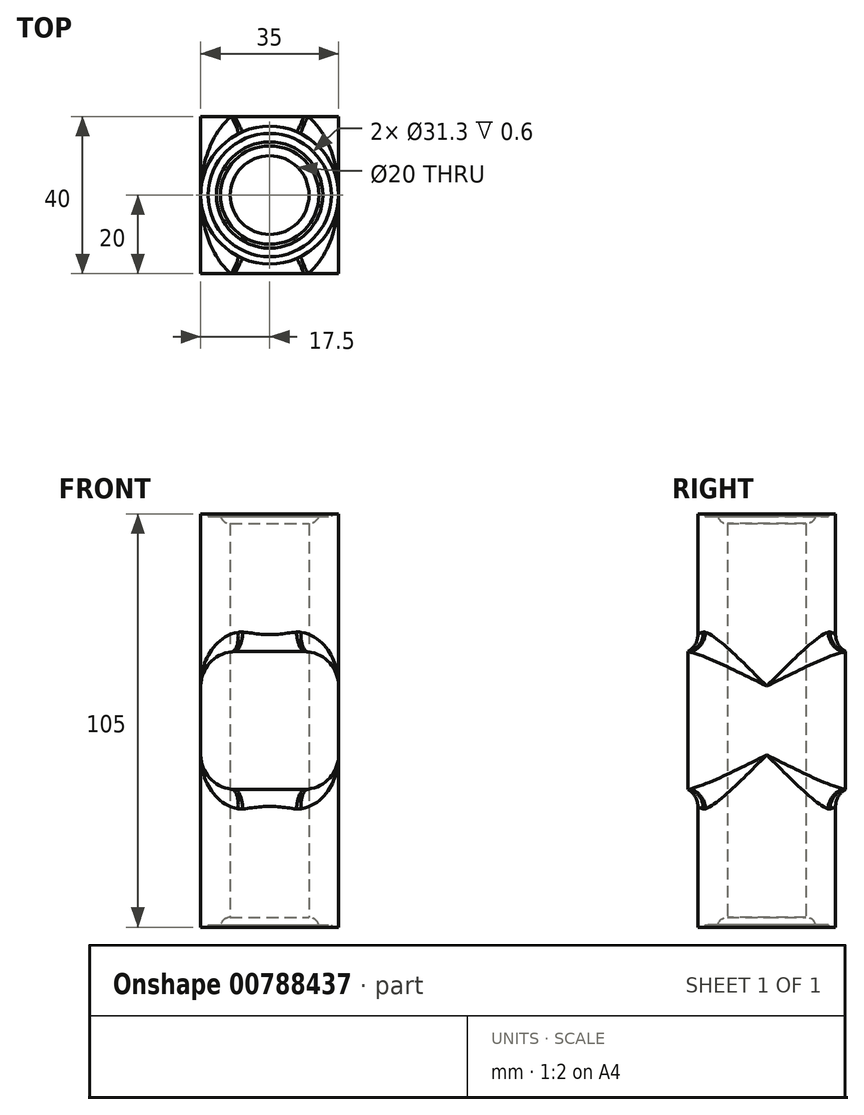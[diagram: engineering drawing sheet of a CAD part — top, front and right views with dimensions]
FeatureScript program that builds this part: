
annotation { "Feature Type Name" : "Feature", "Feature Type Description" : "" }
export const myFeature = defineFeature(function(context is Context, id is Id, definition is map)
    precondition{}
    {
        {
            var Q0;
            Q0=qCreatedBy(makeId("Front.planeOp"),FACE);
            var sketch = newSketch(context, id + "F0", { "sketchPlane" : qUnion([Q0])});
            skLineSegment(sketch, "E0", {"start": v(0, 0) * mm, "end": v(0, 100) * mm, "construction": true});
            skLineSegment(sketch, "E1", {"start": v(0, 0) * mm, "end": v(10, 0) * mm, "construction": true});
            skLineSegment(sketch, "E2", {"start": v(10, 0) * mm, "end": v(10, 100) * mm});
            skLineSegment(sketch, "E3", {"start": v(10, 100) * mm, "end": v(0, 100) * mm, "construction": true});
            skLineSegment(sketch, "E4", {"start": v(10, 100) * mm, "end": v(10, 102.5) * mm, "construction": true});
            skArc(sketch, "E5", {"start": v(10, 100) * mm, "mid": v(11.77, 100.73) * mm, "end": v(12.5, 102.5) * mm});
            skLineSegment(sketch, "E6", {"start": v(12.5, 102.5) * mm, "end": v(13.5, 102.5) * mm});
            skLineSegment(sketch, "E7", {"start": v(13.5, 102.5) * mm, "end": v(13.5, 101.9) * mm});
            skLineSegment(sketch, "E8", {"start": v(13.5, 101.9) * mm, "end": v(15.65, 101.9) * mm});
            skLineSegment(sketch, "E9", {"start": v(15.65, 101.9) * mm, "end": v(15.65, 102.5) * mm});
            skLineSegment(sketch, "E10", {"start": v(15.65, 102.5) * mm, "end": v(17.5, 102.5) * mm});
            skLineSegment(sketch, "E11", {"start": v(17.5, 102.5) * mm, "end": v(17.5, 50) * mm});
            skPoint(sketch, "E11.endSnap0", {"position": v(10, 50) * mm});
            skLineSegment(sketch, "E12", {"start": v(10, 50) * mm, "end": v(17.5, 50) * mm});
            skLineSegment(sketch, "E13.MirrorCS", {"start": v(15.65, -1.9) * mm, "end": v(15.65, -2.5) * mm});
            skLineSegment(sketch, "E14.MirrorCS", {"start": v(15.65, -2.5) * mm, "end": v(17.5, -2.5) * mm});
            skLineSegment(sketch, "E15.MirrorCS", {"start": v(13.5, -2.5) * mm, "end": v(13.5, -1.9) * mm});
            skLineSegment(sketch, "E16.MirrorCS", {"start": v(13.5, -1.9) * mm, "end": v(15.65, -1.9) * mm});
            skLineSegment(sketch, "E17.MirrorCS", {"start": v(12.5, -2.5) * mm, "end": v(13.5, -2.5) * mm});
            skLineSegment(sketch, "E18.MirrorCS", {"start": v(17.5, -2.5) * mm, "end": v(17.5, 50) * mm});
            skArc(sketch, "E19.MirrorCS", {"start": v(10, 0) * mm, "mid": v(11.77, -0.73) * mm, "end": v(12.5, -2.5) * mm});
            skSolve(sketch);
        }
        {
            var Q0;
            {var subQ0=sQuery(id+"F0.wireOp",EDGE,"E5");Q0=makeQuery(id+"F0.imprint","IMPRINT",FACE,{"disambiguationData":[TD([[makeQuery(id+"F0.imprint","IMPRINT",EDGE,{"derivedFrom":subQ0}),-1.0]])]});}
            var Q1;
            {var subQ2=sQuery(id+"F0.wireOp",EDGE,"E12");Q1=makeQuery(id+"F0.imprint","IMPRINT",FACE,{"disambiguationData":[TD([[makeQuery(id+"F0.imprint","IMPRINT",EDGE,{"derivedFrom":subQ2}),-1.0]])]});}
            var Q2;
            Q2=sQuery(id+"F0.wireOp",EDGE,"E0");
            revolve(context, id + "F1", {"surfaceOperationType" : NewSurfaceOperationType.NEW, "entities" : qUnion([Q0, Q1]), "axis" : qUnion([Q2]), "revolveType" : RevolveType.FULL});
        }
        {
            var Q0;
            Q0=qCreatedBy(makeId("Front.planeOp"),FACE);
            cPlane(context, id + "F2", {"entities" : qUnion([Q0]), "cplaneType" : CPlaneType.OFFSET, "offset" : 20 * mm, "width" : 150 * mm, "height" : 150 * mm});
        }
        {
            var Q0;
            Q0=qCreatedBy(id+"F2.planeOp",FACE);
            var sketch = newSketch(context, id + "F3", { "sketchPlane" : qUnion([Q0])});
            skLineSegment(sketch, "E20", {"start": v(-17.5, 102.5) * mm, "end": v(17.5, 102.5) * mm});
            skLineSegment(sketch, "E21", {"start": v(17.5, -2.5) * mm, "end": v(-17.5, -2.5) * mm});
            skLineSegment(sketch, "E22", {"start": v(0, 50) * mm, "end": v(17.5, 50) * mm});
            skLineSegment(sketch, "E23.MirrorCS", {"start": v(8.75, 67.5) * mm, "end": v(0, 67.5) * mm});
            skLineSegment(sketch, "E24.MirrorCS", {"start": v(17.5, 50) * mm, "end": v(17.5, 58.75) * mm});
            skArc(sketch, "E25", {"start": v(8.75, 67.5) * mm, "mid": v(14.94, 64.94) * mm, "end": v(17.5, 58.75) * mm});
            skPoint(sketch, "E25.centerSnap0", {"position": v(8.75, 67.5) * mm});
            skPoint(sketch, "E25.centerSnap1", {"position": v(17.5, 58.75) * mm});
            skPoint(sketch, "E26.orphan", {"position": v(17.5, 67.5) * mm});
            skLineSegment(sketch, "E27.1.0", {"start": v(0, 50) * mm, "end": v(0, 67.5) * mm});
            skPoint(sketch, "E27.1.1", {"position": v(-17.5, 67.5) * mm});
            skPoint(sketch, "E27.1.2", {"position": v(-8.75, 67.5) * mm});
            skPoint(sketch, "E27.1.3", {"position": v(-17.5, 58.75) * mm});
            skLineSegment(sketch, "E27.1.4", {"start": v(-17.5, 58.75) * mm, "end": v(-17.5, 50) * mm});
            skArc(sketch, "E27.1.5", {"start": v(-17.5, 58.75) * mm, "mid": v(-14.94, 64.94) * mm, "end": v(-8.75, 67.5) * mm});
            skLineSegment(sketch, "E27.1.6", {"start": v(0, 67.5) * mm, "end": v(-8.75, 67.5) * mm});
            skPoint(sketch, "E27.1.7", {"position": v(-17.5, 67.5) * mm});
            skLineSegment(sketch, "E27.2.0", {"start": v(0, 50) * mm, "end": v(-17.5, 50) * mm});
            skPoint(sketch, "E27.2.1", {"position": v(-17.5, 32.5) * mm});
            skPoint(sketch, "E27.2.2", {"position": v(-17.5, 41.25) * mm});
            skPoint(sketch, "E27.2.3", {"position": v(-8.75, 32.5) * mm});
            skLineSegment(sketch, "E27.2.4", {"start": v(-8.75, 32.5) * mm, "end": v(0, 32.5) * mm});
            skArc(sketch, "E27.2.5", {"start": v(-8.75, 32.5) * mm, "mid": v(-14.94, 35.06) * mm, "end": v(-17.5, 41.25) * mm});
            skLineSegment(sketch, "E27.2.6", {"start": v(-17.5, 50) * mm, "end": v(-17.5, 41.25) * mm});
            skPoint(sketch, "E27.2.7", {"position": v(-17.5, 32.5) * mm});
            skLineSegment(sketch, "E27.3.0", {"start": v(0, 50) * mm, "end": v(0, 32.5) * mm});
            skPoint(sketch, "E27.3.1", {"position": v(17.5, 32.5) * mm});
            skPoint(sketch, "E27.3.2", {"position": v(8.75, 32.5) * mm});
            skPoint(sketch, "E27.3.3", {"position": v(17.5, 41.25) * mm});
            skLineSegment(sketch, "E27.3.4", {"start": v(17.5, 41.25) * mm, "end": v(17.5, 50) * mm});
            skArc(sketch, "E27.3.5", {"start": v(17.5, 41.25) * mm, "mid": v(14.94, 35.06) * mm, "end": v(8.75, 32.5) * mm});
            skLineSegment(sketch, "E27.3.6", {"start": v(0, 32.5) * mm, "end": v(8.75, 32.5) * mm});
            skPoint(sketch, "E27.3.7", {"position": v(17.5, 32.5) * mm});
            skPoint(sketch, "E27.center", {"position": v(0, 50) * mm});
            skSolve(sketch);
        }
        {
            var Q0;
            Q0=makeQuery(id+"F3.imprint","IMPRINT",FACE,{"disambiguationData":[TD([[makeQuery(id+"F3.imprint","IMPRINT",EDGE,{"derivedFrom":sQuery(id+"F3.wireOp",EDGE,"E27.1.0")}),1.0]])]});
            var Q1;
            Q1=makeQuery(id+"F3.imprint","IMPRINT",FACE,{"disambiguationData":[TD([[makeQuery(id+"F3.imprint","IMPRINT",EDGE,{"derivedFrom":sQuery(id+"F3.wireOp",EDGE,"E22")}),1.0]])]});
            var Q2;
            Q2=makeQuery(id+"F3.imprint","IMPRINT",FACE,{"disambiguationData":[TD([[makeQuery(id+"F3.imprint","IMPRINT",EDGE,{"derivedFrom":sQuery(id+"F3.wireOp",EDGE,"E22")}),-1.0]])]});
            var Q3;
            Q3=makeQuery(id+"F3.imprint","IMPRINT",FACE,{"disambiguationData":[TD([[makeQuery(id+"F3.imprint","IMPRINT",EDGE,{"derivedFrom":sQuery(id+"F3.wireOp",EDGE,"E27.2.0")}),1.0]])]});
            var Q4;
            Q4=makeQuery(id+"F1.opRevolve","SWEPT_FACE",FACE,{"disambiguationData":[OSD([sQuery(id+"F0.wireOp",EDGE,"E11"),sQuery(id+"F0.wireOp",EDGE,"E18.MirrorCS")])]});
            extrude(context, id + "F4", {"entities" : qUnion([Q0, Q1, Q2, Q3]), "operationType" : NewBodyOperationType.ADD, "oppositeDirection" : true, "depth" : 20 * mm, "endBoundEntityFace" : qUnion([Q4]), "offsetDistance" : 25 * mm});
        }
        {
            var Q0;
            Q0=qCreatedBy(makeId("Top.planeOp"),FACE);
            var sketch = newSketch(context, id + "F5", { "sketchPlane" : qUnion([Q0])});
            skCircle(sketch, "E28.0", {"center": v(0, 0) * mm, "radius": 10 * mm});
            skSolve(sketch);
        }
        {
            var Q0;
            Q0 = qSketchRegion(id + "F5", true);
            extrude(context, id + "F6", {"entities" : qUnion([Q0]), "operationType" : NewBodyOperationType.REMOVE, "endBound" : BoundingType.THROUGH_ALL, "depth" : 25 * mm, "offsetDistance" : 25 * mm});
        }
        {
            var Q0;
            Q0=makeQuery(id+"F4.boolean.opBoolean","INTERSECT",EDGE,{"derivedFrom":[makeQuery(id+"F1.opRevolve","SWEPT_FACE",FACE,{"disambiguationData":[OSD([sQuery(id+"F0.wireOp",EDGE,"E11"),sQuery(id+"F0.wireOp",EDGE,"E18.MirrorCS")])]}),makeQuery(id+"F4.opExtrude","SWEPT_FACE",FACE,{"disambiguationData":[OSD([sQuery(id+"F3.wireOp",EDGE,"E27.1.5")])]})]});
            var Q1;
            Q1=makeQuery(id+"F4.boolean.opBoolean","INTERSECT",EDGE,{"derivedFrom":[makeQuery(id+"F1.opRevolve","SWEPT_FACE",FACE,{"disambiguationData":[OSD([sQuery(id+"F0.wireOp",EDGE,"E11"),sQuery(id+"F0.wireOp",EDGE,"E18.MirrorCS")])]}),makeQuery(id+"F4.opExtrude","SWEPT_FACE",FACE,{"disambiguationData":[OSD([sQuery(id+"F3.wireOp",EDGE,"E27.2.5")])]})]});
            fillet(context, id + "F7", {"entities" : qUnion([Q0, Q1]), "radius" : 5 * mm, "tangentPropagation" : true, "allowEdgeOverflow" : false});
        }
        {
            var Q0;
            Q0=makeQuery(id+"F1.opRevolve","SWEPT_BODY",BODY,{"disambiguationData":[OSD([sQuery(id+"F0.wireOp",EDGE,"E2"),sQuery(id+"F0.wireOp",EDGE,"E5"),sQuery(id+"F0.wireOp",EDGE,"E6"),sQuery(id+"F0.wireOp",EDGE,"E7"),sQuery(id+"F0.wireOp",EDGE,"E8"),sQuery(id+"F0.wireOp",EDGE,"E9"),sQuery(id+"F0.wireOp",EDGE,"E10"),sQuery(id+"F0.wireOp",EDGE,"E11"),sQuery(id+"F0.wireOp",EDGE,"E13.MirrorCS"),sQuery(id+"F0.wireOp",EDGE,"E14.MirrorCS"),sQuery(id+"F0.wireOp",EDGE,"E15.MirrorCS"),sQuery(id+"F0.wireOp",EDGE,"E16.MirrorCS"),sQuery(id+"F0.wireOp",EDGE,"E17.MirrorCS"),sQuery(id+"F0.wireOp",EDGE,"E18.MirrorCS"),sQuery(id+"F0.wireOp",EDGE,"E19.MirrorCS")])]});
            var Q1;
            Q1=qCreatedBy(makeId("Front.planeOp"),FACE);
            mirror(context, id + "F8", {"operationType" : NewBodyOperationType.ADD, "entities" : qUnion([Q0]), "mirrorPlane" : qUnion([Q1])});
        }
    });
